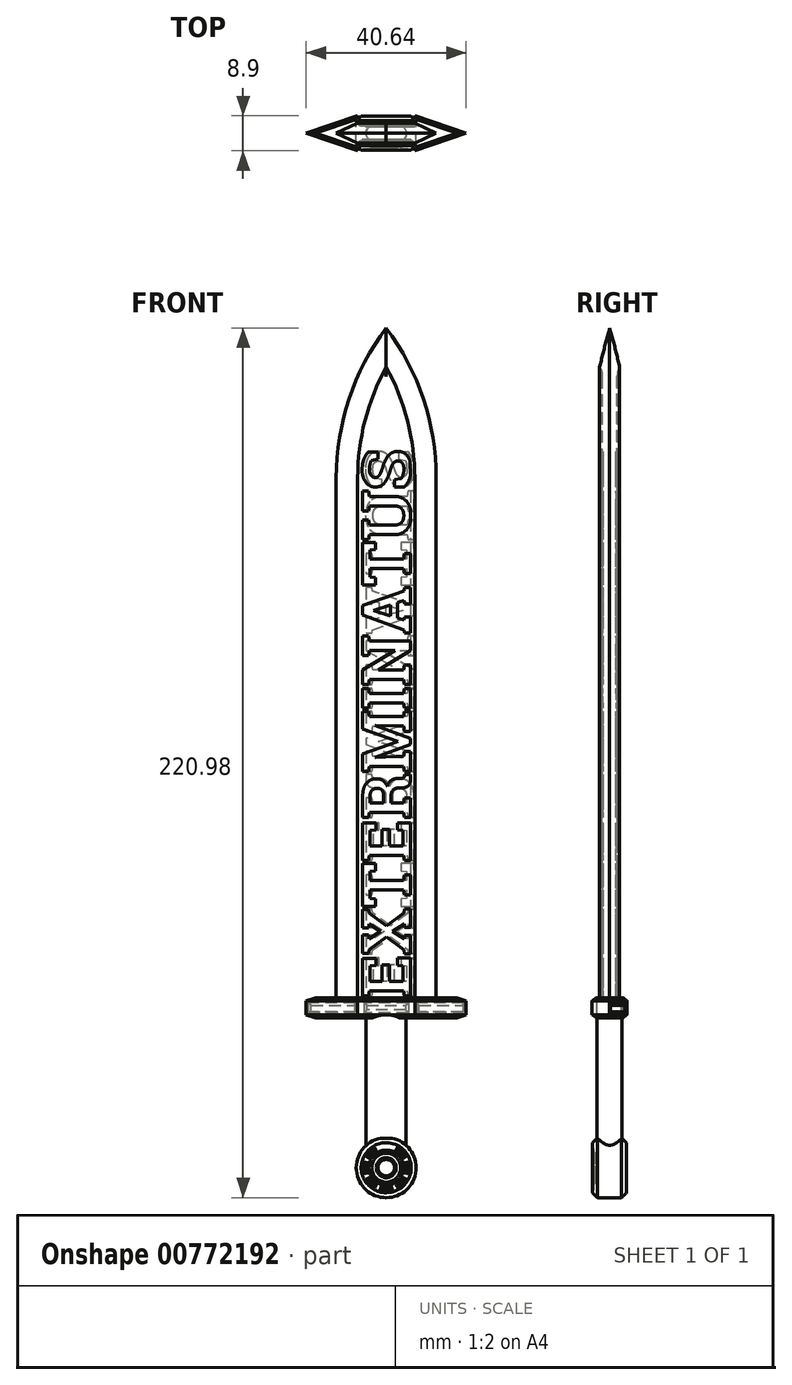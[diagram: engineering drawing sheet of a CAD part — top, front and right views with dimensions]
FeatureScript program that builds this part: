
annotation { "Feature Type Name" : "Feature", "Feature Type Description" : "" }
export const myFeature = defineFeature(function(context is Context, id is Id, definition is map)
    precondition{}
    {
        {
            var Q0;
            Q0=qCreatedBy(makeId("Front.planeOp"),FACE);
            var sketch = newSketch(context, id + "F0", { "sketchPlane" : qUnion([Q0])});
            skLineSegment(sketch, "E0.bottom", {"start": v(-51.68, 0) * mm, "end": v(-26.28, 0) * mm});
            skLineSegment(sketch, "E0.top", {"start": v(-51.68, 132.08) * mm, "end": v(-26.28, 132.08) * mm});
            skLineSegment(sketch, "E0.left", {"start": v(-51.68, 0) * mm, "end": v(-51.68, 132.08) * mm});
            skLineSegment(sketch, "E0.right", {"start": v(-26.28, 0) * mm, "end": v(-26.28, 132.08) * mm});
            skLineSegment(sketch, "E1", {"start": v(-38.98, 132.08) * mm, "end": v(-38.98, 170.18) * mm});
            skArc(sketch, "E2", {"start": v(-38.98, 170.18) * mm, "mid": v(-48.42, 152.16) * mm, "end": v(-51.68, 132.08) * mm});
            skArc(sketch, "E3", {"start": v(-26.28, 132.08) * mm, "mid": v(-29.54, 152.16) * mm, "end": v(-38.98, 170.18) * mm});
            skSolve(sketch);
        }
        {
            var Q0;
            Q0 = qSketchRegion(id + "F0", true);
            extrude(context, id + "F1", {"entities" : qUnion([Q0]), "endBound" : BoundingType.SYMMETRIC, "oppositeDirection" : true, "depth" : 5.08 * mm, "offsetDistance" : 25.4 * mm});
        }
        {
            var Q0;
            Q0=makeQuery(id+"F1.opExtrude","CAP_EDGE",EDGE,{"disambiguationData":[OSD([sQuery(id+"F0.wireOp",EDGE,"E3")])],"isStart":true});
            var Q1;
            Q1=makeQuery(id+"F1.opExtrude","CAP_EDGE",EDGE,{"disambiguationData":[OSD([sQuery(id+"F0.wireOp",EDGE,"E2")])],"isStart":true});
            chamfer(context, id + "F2", {"entities" : qUnion([Q0, Q1]), "chamferType" : ChamferType.OFFSET_ANGLE, "width" : 2.54 * mm, "oppositeDirection" : true, "angle" : 65 * degree, "tangentPropagation" : true});
        }
        {
            var Q0;
            Q0=makeQuery(id+"F1.opExtrude","CAP_EDGE",EDGE,{"disambiguationData":[OSD([sQuery(id+"F0.wireOp",EDGE,"E3")])],"isStart":false});
            var Q1;
            Q1=makeQuery(id+"F1.opExtrude","CAP_EDGE",EDGE,{"disambiguationData":[OSD([sQuery(id+"F0.wireOp",EDGE,"E2")])],"isStart":false});
            chamfer(context, id + "F3", {"entities" : qUnion([Q0, Q1]), "chamferType" : ChamferType.OFFSET_ANGLE, "width" : 2.54 * mm, "oppositeDirection" : false, "angle" : 65 * degree, "tangentPropagation" : true});
        }
        {
            var Q0;
            Q0=makeQuery(id+"F1.opExtrude","CAP_FACE",FACE,{"disambiguationData":[OSD([sQuery(id+"F0.wireOp",EDGE,"E0.bottom"),sQuery(id+"F0.wireOp",EDGE,"E0.left"),sQuery(id+"F0.wireOp",EDGE,"E0.right"),sQuery(id+"F0.wireOp",EDGE,"E2"),sQuery(id+"F0.wireOp",EDGE,"E3")])],"isStart":false});
            var sketch = newSketch(context, id + "F4", { "sketchPlane" : qUnion([Q0])});
            skLineSegment(sketch, "E4.0.0", {"start": v(31.72, 0) * mm, "end": v(46.23, 0) * mm});
            skLineSegment(sketch, "E4.0.1", {"start": v(46.23, 0) * mm, "end": v(46.23, 132.08) * mm});
            skArc(sketch, "E4.0.2", {"start": v(46.23, 132.08) * mm, "mid": v(44.39, 146.59) * mm, "end": v(38.98, 160.18) * mm});
            skArc(sketch, "E4.0.3", {"start": v(38.98, 160.18) * mm, "mid": v(33.57, 146.59) * mm, "end": v(31.72, 132.08) * mm});
            skLineSegment(sketch, "E4.0.4", {"start": v(31.72, 132.08) * mm, "end": v(31.72, 0) * mm});
            skSolve(sketch);
        }
        {
            var Q0;
            Q0 = qSketchRegion(id + "F4", true);
            extrude(context, id + "F5", {"entities" : qUnion([Q0]), "operationType" : NewBodyOperationType.REMOVE, "oppositeDirection" : true, "depth" : 0.64 * mm, "offsetDistance" : 25.4 * mm});
        }
        {
            var Q0;
            Q0=makeQuery(id+"F1.opExtrude","CAP_FACE",FACE,{"disambiguationData":[OSD([sQuery(id+"F0.wireOp",EDGE,"E0.bottom"),sQuery(id+"F0.wireOp",EDGE,"E0.left"),sQuery(id+"F0.wireOp",EDGE,"E0.right"),sQuery(id+"F0.wireOp",EDGE,"E2"),sQuery(id+"F0.wireOp",EDGE,"E3")])],"isStart":true});
            var sketch = newSketch(context, id + "F6", { "sketchPlane" : qUnion([Q0])});
            skArc(sketch, "E5.0.0", {"start": v(-38.98, 160.18) * mm, "mid": v(-44.39, 146.59) * mm, "end": v(-46.23, 132.08) * mm});
            skLineSegment(sketch, "E5.0.1", {"start": v(-46.23, 132.08) * mm, "end": v(-46.23, 0) * mm});
            skLineSegment(sketch, "E5.0.2", {"start": v(-46.23, 0) * mm, "end": v(-31.72, 0) * mm});
            skLineSegment(sketch, "E5.0.3", {"start": v(-31.72, 0) * mm, "end": v(-31.72, 132.08) * mm});
            skArc(sketch, "E5.0.4", {"start": v(-31.72, 132.08) * mm, "mid": v(-33.57, 146.59) * mm, "end": v(-38.98, 160.18) * mm});
            skSolve(sketch);
        }
        {
            var Q0;
            Q0 = qSketchRegion(id + "F6", true);
            extrude(context, id + "F7", {"entities" : qUnion([Q0]), "operationType" : NewBodyOperationType.REMOVE, "oppositeDirection" : true, "depth" : 0.64 * mm, "offsetDistance" : 25.4 * mm});
        }
        {
            var Q0;
            Q0=makeQuery(id+"F7.boolean.opBoolean","COPY",EDGE,{"derivedFrom":makeQuery(id+"F7.opExtrude","CAP_EDGE",EDGE,{"disambiguationData":[OSD([sQuery(id+"F6.wireOp",EDGE,"E5.0.3")])],"isStart":false})});
            var Q1;
            Q1=makeQuery(id+"F7.boolean.opBoolean","COPY",EDGE,{"derivedFrom":makeQuery(id+"F7.opExtrude","CAP_EDGE",EDGE,{"disambiguationData":[OSD([sQuery(id+"F6.wireOp",EDGE,"E5.0.1")])],"isStart":false})});
            fillet(context, id + "F8", {"entities" : qUnion([Q0, Q1]), "radius" : 1.27 * mm, "tangentPropagation" : true, "allowEdgeOverflow" : false});
        }
        {
            var Q0;
            Q0=makeQuery(id+"F5.boolean.opBoolean","COPY",EDGE,{"derivedFrom":makeQuery(id+"F5.opExtrude","CAP_EDGE",EDGE,{"disambiguationData":[OSD([sQuery(id+"F4.wireOp",EDGE,"E4.0.1")])],"isStart":false})});
            var Q1;
            Q1=makeQuery(id+"F5.boolean.opBoolean","COPY",EDGE,{"derivedFrom":makeQuery(id+"F5.opExtrude","CAP_EDGE",EDGE,{"disambiguationData":[OSD([sQuery(id+"F4.wireOp",EDGE,"E4.0.4")])],"isStart":false})});
            fillet(context, id + "F9", {"entities" : qUnion([Q0, Q1]), "radius" : 1.27 * mm, "tangentPropagation" : true, "allowEdgeOverflow" : false});
        }
        {
            var Q0;
            Q0=makeQuery(id+"F7.boolean.opBoolean","COPY",FACE,{"derivedFrom":makeQuery(id+"F7.opExtrude","CAP_FACE",FACE,{"disambiguationData":[OSD([sQuery(id+"F6.wireOp",EDGE,"E5.0.0"),sQuery(id+"F6.wireOp",EDGE,"E5.0.1"),sQuery(id+"F6.wireOp",EDGE,"E5.0.2"),sQuery(id+"F6.wireOp",EDGE,"E5.0.3"),sQuery(id+"F6.wireOp",EDGE,"E5.0.4")])],"isStart":false})});
            var sketch = newSketch(context, id + "F10", { "sketchPlane" : qUnion([Q0])});
            skText(sketch, "E6", { "text": "EXTERMINATUS\n", "fontName": "RobotoSlab-Bold.ttf"});
            const initialGuessF10  = {"E6": [-0.03282, 0, 0, 1, 0.0123]};
            skSetInitialGuess(sketch, initialGuessF10);
            skSolve(sketch);
        }
        {
            var Q0;
            Q0 = qSketchRegion(id + "F10", true);
            extrude(context, id + "F11", {"entities" : qUnion([Q0]), "operationType" : NewBodyOperationType.REMOVE, "oppositeDirection" : true, "depth" : 0.25 * mm, "offsetDistance" : 25.4 * mm});
        }
        {
            var Q0;
            Q0=makeQuery(id+"F5.boolean.opBoolean","COPY",FACE,{"derivedFrom":makeQuery(id+"F5.opExtrude","CAP_FACE",FACE,{"disambiguationData":[OSD([sQuery(id+"F4.wireOp",EDGE,"E4.0.0"),sQuery(id+"F4.wireOp",EDGE,"E4.0.1"),sQuery(id+"F4.wireOp",EDGE,"E4.0.2"),sQuery(id+"F4.wireOp",EDGE,"E4.0.3"),sQuery(id+"F4.wireOp",EDGE,"E4.0.4")])],"isStart":false})});
            var sketch = newSketch(context, id + "F12", { "sketchPlane" : qUnion([Q0])});
            skText(sketch, "E7", { "text": "EXTERMINATUS", "fontName": "RobotoSlab-Bold.ttf"});
            const initialGuessF12  = {"E7": [0.04408, 0, 0, 1, 0.0123]};
            skSetInitialGuess(sketch, initialGuessF12);
            skSolve(sketch);
        }
        {
            var Q0;
            Q0 = qSketchRegion(id + "F12", true);
            extrude(context, id + "F13", {"entities" : qUnion([Q0]), "operationType" : NewBodyOperationType.REMOVE, "oppositeDirection" : true, "depth" : 0.25 * mm, "offsetDistance" : 25.4 * mm});
        }
        {
            var Q0;
            Q0=makeQuery(id+"F1.opExtrude","SWEPT_FACE",FACE,{"disambiguationData":[OSD([sQuery(id+"F0.wireOp",EDGE,"E0.bottom")])]});
            var sketch = newSketch(context, id + "F14", { "sketchPlane" : qUnion([Q0])});
            skLineSegment(sketch, "E8.0.0", {"start": v(-32.82, 1.9) * mm, "end": v(-45.13, 1.9) * mm});
            skArc(sketch, "E8.0.1", {"start": v(-45.13, 1.9) * mm, "mid": v(-45.77, 2.08) * mm, "end": v(-46.23, 2.54) * mm});
            skLineSegment(sketch, "E8.0.2", {"start": v(-46.23, 2.54) * mm, "end": v(-51.68, 0) * mm});
            skLineSegment(sketch, "E8.0.3", {"start": v(-51.68, 0) * mm, "end": v(-46.23, -2.54) * mm});
            skArc(sketch, "E8.0.4", {"start": v(-46.23, -2.54) * mm, "mid": v(-45.77, -2.08) * mm, "end": v(-45.13, -1.9) * mm});
            skLineSegment(sketch, "E8.0.5", {"start": v(-45.13, -1.9) * mm, "end": v(-32.82, -1.9) * mm});
            skArc(sketch, "E8.0.6", {"start": v(-32.82, -1.9) * mm, "mid": v(-32.19, -2.08) * mm, "end": v(-31.72, -2.54) * mm});
            skLineSegment(sketch, "E8.0.7", {"start": v(-31.72, -2.54) * mm, "end": v(-26.28, 0) * mm});
            skLineSegment(sketch, "E8.0.8", {"start": v(-26.28, 0) * mm, "end": v(-31.72, 2.54) * mm});
            skArc(sketch, "E8.0.9", {"start": v(-31.72, 2.54) * mm, "mid": v(-32.19, 2.08) * mm, "end": v(-32.82, 1.9) * mm});
            skLineSegment(sketch, "E9.bottom", {"start": v(-59.3, -4.45) * mm, "end": v(-18.66, -4.44) * mm});
            skLineSegment(sketch, "E9.top", {"start": v(-59.3, 4.45) * mm, "end": v(-18.66, 4.45) * mm});
            skLineSegment(sketch, "E9.left", {"start": v(-59.3, -4.45) * mm, "end": v(-59.3, 4.45) * mm});
            skLineSegment(sketch, "E9.right", {"start": v(-18.66, -4.44) * mm, "end": v(-18.66, 4.45) * mm});
            skPoint(sketch, "E10.start.orphan", {"position": v(-59.3, 0) * mm});
            skLineSegment(sketch, "E11", {"start": v(-59.3, 0) * mm, "end": v(-46.23, 4.45) * mm});
            skLineSegment(sketch, "E12", {"start": v(-38.98, 1.9) * mm, "end": v(-38.98, 0.5) * mm});
            skLineSegment(sketch, "E13", {"start": v(-43.87, 0) * mm, "end": v(-41.2, 0) * mm});
            skLineSegment(sketch, "E14", {"start": v(-45.13, 3.18) * mm, "end": v(-32.82, 3.18) * mm});
            skLineSegment(sketch, "E15", {"start": v(-32.82, -3.18) * mm, "end": v(-45.13, -3.18) * mm});
            skLineSegment(sketch, "E16.MirrorCS", {"start": v(-18.66, 0) * mm, "end": v(-31.72, 4.45) * mm});
            skArc(sketch, "E17", {"start": v(-46.23, 4.45) * mm, "mid": v(-45.97, 3.56) * mm, "end": v(-45.13, 3.18) * mm});
            skArc(sketch, "E18.MirrorCS", {"start": v(-31.72, 4.45) * mm, "mid": v(-31.98, 3.56) * mm, "end": v(-32.82, 3.18) * mm});
            skArc(sketch, "E19.MirrorCS", {"start": v(-46.23, -4.45) * mm, "mid": v(-45.97, -3.56) * mm, "end": v(-45.13, -3.18) * mm});
            skArc(sketch, "E20.MirrorCS", {"start": v(-31.72, -4.45) * mm, "mid": v(-31.98, -3.56) * mm, "end": v(-32.82, -3.18) * mm});
            skLineSegment(sketch, "E21.MirrorCS", {"start": v(-59.3, 0) * mm, "end": v(-46.23, -4.45) * mm});
            skLineSegment(sketch, "E22.MirrorCS", {"start": v(-18.66, 0) * mm, "end": v(-31.72, -4.45) * mm});
            skSolve(sketch);
        }
        {
            var Q0;
            {var subQ0=sQuery(id+"F14.wireOp",EDGE,"E8.0.1");Q0=makeQuery(id+"F14.imprint","IMPRINT",FACE,{"disambiguationData":[TD([[makeQuery(id+"F14.imprint","IMPRINT",EDGE,{"derivedFrom":subQ0}),-1.0]])]});}
            var Q1;
            {var subQ0=sQuery(id+"F14.wireOp",EDGE,"E8.0.1");Q1=makeQuery(id+"F14.imprint","IMPRINT",FACE,{"disambiguationData":[TD([[makeQuery(id+"F14.imprint","IMPRINT",EDGE,{"derivedFrom":subQ0}),1.0]])]});}
            extrude(context, id + "F15", {"entities" : qUnion([Q0, Q1]), "operationType" : NewBodyOperationType.ADD, "depth" : 5.08 * mm, "offsetDistance" : 25.4 * mm});
        }
        {
            var Q0;
            Q0=makeQuery(id+"F15.opExtrude","CAP_EDGE",EDGE,{"disambiguationData":[OSD([sQuery(id+"F14.wireOp",EDGE,"E22.MirrorCS")])],"isStart":true});
            var Q1;
            Q1=makeQuery(id+"F15.opExtrude","CAP_EDGE",EDGE,{"disambiguationData":[OSD([sQuery(id+"F14.wireOp",EDGE,"E15")])],"isStart":true});
            var Q2;
            Q2=makeQuery(id+"F15.opExtrude","CAP_EDGE",EDGE,{"disambiguationData":[OSD([sQuery(id+"F14.wireOp",EDGE,"E21.MirrorCS")])],"isStart":true});
            var Q3;
            Q3=makeQuery(id+"F15.opExtrude","CAP_EDGE",EDGE,{"disambiguationData":[OSD([sQuery(id+"F14.wireOp",EDGE,"E11")])],"isStart":true});
            var Q4;
            Q4=makeQuery(id+"F15.opExtrude","CAP_EDGE",EDGE,{"disambiguationData":[OSD([sQuery(id+"F14.wireOp",EDGE,"E14")])],"isStart":true});
            var Q5;
            Q5=makeQuery(id+"F15.opExtrude","CAP_EDGE",EDGE,{"disambiguationData":[OSD([sQuery(id+"F14.wireOp",EDGE,"E16.MirrorCS")])],"isStart":true});
            var Q6;
            Q6=makeQuery(id+"F15.opExtrude","CAP_FACE",FACE,{"disambiguationData":[OSD([sQuery(id+"F14.wireOp",EDGE,"E11"),sQuery(id+"F14.wireOp",EDGE,"E14"),sQuery(id+"F14.wireOp",EDGE,"E15"),sQuery(id+"F14.wireOp",EDGE,"E16.MirrorCS"),sQuery(id+"F14.wireOp",EDGE,"E17"),sQuery(id+"F14.wireOp",EDGE,"E18.MirrorCS"),sQuery(id+"F14.wireOp",EDGE,"E19.MirrorCS"),sQuery(id+"F14.wireOp",EDGE,"E20.MirrorCS"),sQuery(id+"F14.wireOp",EDGE,"E21.MirrorCS"),sQuery(id+"F14.wireOp",EDGE,"E22.MirrorCS")])],"isStart":false});
            chamfer(context, id + "F16", {"entities" : qUnion([Q0, Q1, Q2, Q3, Q4, Q5, Q6]), "width" : 0.76 * mm, "tangentPropagation" : true});
        }
        {
            var Q0;
            Q0=makeQuery(id+"F15.opExtrude","CAP_FACE",FACE,{"disambiguationData":[OSD([sQuery(id+"F14.wireOp",EDGE,"E11"),sQuery(id+"F14.wireOp",EDGE,"E14"),sQuery(id+"F14.wireOp",EDGE,"E15"),sQuery(id+"F14.wireOp",EDGE,"E16.MirrorCS"),sQuery(id+"F14.wireOp",EDGE,"E17"),sQuery(id+"F14.wireOp",EDGE,"E18.MirrorCS"),sQuery(id+"F14.wireOp",EDGE,"E19.MirrorCS"),sQuery(id+"F14.wireOp",EDGE,"E20.MirrorCS"),sQuery(id+"F14.wireOp",EDGE,"E21.MirrorCS"),sQuery(id+"F14.wireOp",EDGE,"E22.MirrorCS")])],"isStart":false});
            var sketch = newSketch(context, id + "F17", { "sketchPlane" : qUnion([Q0])});
            skArc(sketch, "E23.0.0", {"start": v(-32.82, -2.41) * mm, "mid": v(-31.84, -2.7) * mm, "end": v(-31.15, -3.44) * mm});
            skLineSegment(sketch, "E23.0.1", {"start": v(-31.15, -3.44) * mm, "end": v(-21.02, 0) * mm});
            skLineSegment(sketch, "E23.0.2", {"start": v(-21.02, 0) * mm, "end": v(-31.15, 3.44) * mm});
            skArc(sketch, "E23.0.3", {"start": v(-31.15, 3.44) * mm, "mid": v(-31.84, 2.7) * mm, "end": v(-32.82, 2.41) * mm});
            skLineSegment(sketch, "E23.0.4", {"start": v(-32.82, 2.41) * mm, "end": v(-45.13, 2.41) * mm});
            skArc(sketch, "E23.0.5", {"start": v(-45.13, 2.41) * mm, "mid": v(-46.11, 2.7) * mm, "end": v(-46.8, 3.44) * mm});
            skLineSegment(sketch, "E23.0.6", {"start": v(-46.8, 3.44) * mm, "end": v(-56.93, 0) * mm});
            skLineSegment(sketch, "E23.0.7", {"start": v(-56.93, 0) * mm, "end": v(-46.8, -3.44) * mm});
            skArc(sketch, "E23.0.8", {"start": v(-46.8, -3.44) * mm, "mid": v(-46.11, -2.7) * mm, "end": v(-45.13, -2.41) * mm});
            skLineSegment(sketch, "E23.0.9", {"start": v(-45.13, -2.41) * mm, "end": v(-32.82, -2.41) * mm});
            skPoint(sketch, "E24.centerSnap0", {"position": v(-38.98, -2.41) * mm});
            skPoint(sketch, "E24.center.orphan", {"position": v(-38.98, 0) * mm});
            skEllipse(sketch, "E25", {"center": v(-38.98, 0) * mm, "majorRadius": 5.08 * mm, "minorRadius": 3.18 * mm, "majorAxis": v(-1, 0)});
            skSolve(sketch);
        }
        {
            var Q0;
            {var subQ0=sQuery(id+"F17.wireOp",EDGE,"E25");var subQ1=sQuery(id+"F17.wireOp",EDGE,"E23.0.4");var subQ2=makeQuery(id+"F17.imprint","INTERSECT",VERTEX,{"disambiguationData":[OD(0.0)],"derivedFrom":[subQ1,subQ0]});Q0=makeQuery(id+"F17.imprint","IMPRINT",FACE,{"disambiguationData":[TD([[makeQuery(id+"F17.imprint","IMPRINT",EDGE,{"disambiguationData":[TD([[subQ2,-1.0]])],"derivedFrom":subQ1}),1.0]])]});}
            var Q1;
            {var subQ0=sQuery(id+"F17.wireOp",EDGE,"E25");var subQ1=sQuery(id+"F17.wireOp",EDGE,"E23.0.4");var subQ2=makeQuery(id+"F17.imprint","INTERSECT",VERTEX,{"disambiguationData":[OD(0.0)],"derivedFrom":[subQ1,subQ0]});Q1=makeQuery(id+"F17.imprint","IMPRINT",FACE,{"disambiguationData":[TD([[makeQuery(id+"F17.imprint","IMPRINT",EDGE,{"disambiguationData":[TD([[subQ2,-1.0]])],"derivedFrom":subQ1}),-1.0]])]});}
            var Q2;
            {var subQ0=sQuery(id+"F17.wireOp",EDGE,"E25");var subQ1=sQuery(id+"F17.wireOp",EDGE,"E23.0.9");var subQ2=makeQuery(id+"F17.imprint","INTERSECT",VERTEX,{"disambiguationData":[OD(0.0)],"derivedFrom":[subQ1,subQ0]});Q2=makeQuery(id+"F17.imprint","IMPRINT",FACE,{"disambiguationData":[TD([[makeQuery(id+"F17.imprint","IMPRINT",EDGE,{"disambiguationData":[TD([[subQ2,-1.0]])],"derivedFrom":subQ1}),-1.0]])]});}
            extrude(context, id + "F18", {"entities" : qUnion([Q0, Q1, Q2]), "operationType" : NewBodyOperationType.ADD, "depth" : 38.1 * mm, "offsetDistance" : 25.4 * mm});
        }
        {
            var Q0;
            {var subQ0=sQuery(id+"F14.wireOp",EDGE,"E14");var subQ1=sQuery(id+"F17.wireOp",EDGE,"E25");Q0=makeQuery(id+"F18.boolean.opBoolean","SPLIT",FACE,{"disambiguationData":[TD([makeQuery(id+"F16.opChamfer","BLEND_FACE",FACE,{"disambiguationData":[OSD([subQ0]),TDD([makeQuery(id+"F15.opExtrude","CAP_EDGE",EDGE,{"disambiguationData":[OSD([subQ0])],"isStart":false})])]})])],"derivedFrom":makeQuery(id+"F18.opExtrude","CAP_FACE",FACE,{"disambiguationData":[OSD([subQ1])],"isStart":true})});}
            var sketch = newSketch(context, id + "F19", { "sketchPlane" : qUnion([Q0])});
            skEllipticalArc(sketch, "E26.0", {});
            skLineSegment(sketch, "E27.0.1", {"start": v(-35.68, -2.41) * mm, "end": v(-42.28, -2.41) * mm});
            skEllipticalArc(sketch, "E28.0.0", {});
            skLineSegment(sketch, "E28.0.1", {"start": v(-42.28, 2.41) * mm, "end": v(-35.68, 2.41) * mm});
            const initialGuessF19  = {"E26.0": [-0.03897777617146298, 0, -1, 0, 0.00508, 0.003175, 0.8633131150155545, 2.278279538574239], "E26.0": [-0.03897777617146298, 0, -1, 0, 0.00508, 0.003175, 0.8633131150155545, 2.278279538574239], "E28.0.0": [-0.03897777617146298, 0, -1, 0, 0.00508, 0.003175, 4.004905768605347, 5.419872192164032]};
            skSetInitialGuess(sketch, initialGuessF19);
            skSolve(sketch);
        }
        {
            var Q0;
            Q0 = qSketchRegion(id + "F19", true);
            extrude(context, id + "F20", {"entities" : qUnion([Q0]), "operationType" : NewBodyOperationType.ADD, "depth" : 0.76 * mm, "offsetDistance" : 25.4 * mm});
        }
        {
            var Q0;
            Q0=makeQuery(id+"F15.opExtrude","SWEPT_FACE",FACE,{"disambiguationData":[OSD([sQuery(id+"F14.wireOp",EDGE,"E15")])]});
            var sketch = newSketch(context, id + "F21", { "sketchPlane" : qUnion([Q0])});
            skLineSegment(sketch, "E29.0.0", {"start": v(32.82, -0.76) * mm, "end": v(32.82, -4.32) * mm});
            skLineSegment(sketch, "E29.0.1", {"start": v(32.82, -4.32) * mm, "end": v(38.98, -4.32) * mm});
            skLineSegment(sketch, "E29.0.2", {"start": v(38.98, -4.32) * mm, "end": v(45.13, -4.32) * mm});
            skLineSegment(sketch, "E29.0.3", {"start": v(45.13, -4.32) * mm, "end": v(45.13, -0.76) * mm});
            skLineSegment(sketch, "E29.0.4", {"start": v(45.13, -0.76) * mm, "end": v(32.82, -0.76) * mm});
            skLineSegment(sketch, "E30.bottom", {"start": v(33.33, -1.27) * mm, "end": v(44.62, -1.27) * mm});
            skLineSegment(sketch, "E30.top", {"start": v(33.33, -3.81) * mm, "end": v(44.62, -3.8) * mm});
            skLineSegment(sketch, "E30.left", {"start": v(33.33, -1.27) * mm, "end": v(33.33, -3.81) * mm});
            skLineSegment(sketch, "E30.right", {"start": v(44.62, -1.27) * mm, "end": v(44.62, -3.8) * mm});
            skSolve(sketch);
        }
        {
            var Q0;
            Q0=makeQuery(id+"F21.imprint","IMPRINT",FACE,{"disambiguationData":[TD([[makeQuery(id+"F21.imprint","IMPRINT",EDGE,{"derivedFrom":sQuery(id+"F21.wireOp",EDGE,"E30.bottom")}),-1.0]])]});
            extrude(context, id + "F22", {"entities" : qUnion([Q0]), "operationType" : NewBodyOperationType.REMOVE, "oppositeDirection" : true, "depth" : 0.25 * mm, "offsetDistance" : 25.4 * mm});
        }
        {
            var Q0;
            Q0=makeQuery(id+"F15.opExtrude","SWEPT_FACE",FACE,{"disambiguationData":[OSD([sQuery(id+"F14.wireOp",EDGE,"E22.MirrorCS")])]});
            var sketch = newSketch(context, id + "F23", { "sketchPlane" : qUnion([Q0])});
            skLineSegment(sketch, "E31.bottom", {"start": v(18.17, -1.27) * mm, "end": v(30.96, -1.27) * mm});
            skLineSegment(sketch, "E31.top", {"start": v(18.17, -3.81) * mm, "end": v(30.96, -3.81) * mm});
            skLineSegment(sketch, "E31.left", {"start": v(18.17, -1.27) * mm, "end": v(18.17, -3.81) * mm});
            skLineSegment(sketch, "E31.right", {"start": v(30.96, -1.27) * mm, "end": v(30.96, -3.81) * mm});
            skSolve(sketch);
        }
        {
            var Q0;
            Q0 = qSketchRegion(id + "F23", true);
            extrude(context, id + "F24", {"entities" : qUnion([Q0]), "operationType" : NewBodyOperationType.REMOVE, "oppositeDirection" : true, "depth" : 0.25 * mm, "offsetDistance" : 25.4 * mm});
        }
        {
            var Q0;
            Q0=makeQuery(id+"F15.opExtrude","SWEPT_FACE",FACE,{"disambiguationData":[OSD([sQuery(id+"F14.wireOp",EDGE,"E21.MirrorCS")])]});
            var sketch = newSketch(context, id + "F25", { "sketchPlane" : qUnion([Q0])});
            skLineSegment(sketch, "E32.bottom", {"start": v(42.84, -1.27) * mm, "end": v(55.63, -1.27) * mm});
            skLineSegment(sketch, "E32.top", {"start": v(42.84, -3.81) * mm, "end": v(55.63, -3.8) * mm});
            skLineSegment(sketch, "E32.left", {"start": v(42.84, -1.27) * mm, "end": v(42.84, -3.81) * mm});
            skLineSegment(sketch, "E32.right", {"start": v(55.63, -1.27) * mm, "end": v(55.63, -3.8) * mm});
            skSolve(sketch);
        }
        {
            var Q0;
            Q0 = qSketchRegion(id + "F25", true);
            extrude(context, id + "F26", {"entities" : qUnion([Q0]), "operationType" : NewBodyOperationType.REMOVE, "oppositeDirection" : true, "depth" : 0.25 * mm, "offsetDistance" : 25.4 * mm});
        }
        {
            var Q0;
            Q0=makeQuery(id+"F22.boolean.opBoolean","COPY",FACE,{"derivedFrom":makeQuery(id+"F22.opExtrude","CAP_FACE",FACE,{"disambiguationData":[OSD([sQuery(id+"F21.wireOp",EDGE,"E30.bottom"),sQuery(id+"F21.wireOp",EDGE,"E30.top"),sQuery(id+"F21.wireOp",EDGE,"E30.left"),sQuery(id+"F21.wireOp",EDGE,"E30.right")])],"isStart":false})});
            var Q1;
            Q1=makeQuery(id+"F26.boolean.opBoolean","COPY",FACE,{"derivedFrom":makeQuery(id+"F26.opExtrude","CAP_FACE",FACE,{"disambiguationData":[OSD([sQuery(id+"F25.wireOp",EDGE,"E32.bottom"),sQuery(id+"F25.wireOp",EDGE,"E32.top"),sQuery(id+"F25.wireOp",EDGE,"E32.left"),sQuery(id+"F25.wireOp",EDGE,"E32.right")])],"isStart":false})});
            var Q2;
            Q2=makeQuery(id+"F24.boolean.opBoolean","COPY",FACE,{"derivedFrom":makeQuery(id+"F24.opExtrude","CAP_FACE",FACE,{"disambiguationData":[OSD([sQuery(id+"F23.wireOp",EDGE,"E31.bottom"),sQuery(id+"F23.wireOp",EDGE,"E31.top"),sQuery(id+"F23.wireOp",EDGE,"E31.left"),sQuery(id+"F23.wireOp",EDGE,"E31.right")])],"isStart":false})});
            chamfer(context, id + "F27", {"entities" : qUnion([Q0, Q1, Q2]), "chamferType" : ChamferType.OFFSET_ANGLE, "width" : 0.25 * mm, "oppositeDirection" : false, "angle" : 70 * degree, "tangentPropagation" : true});
        }
        {
            var Q0;
            Q0=qCreatedBy(makeId("Front.planeOp"),FACE);
            var sketch = newSketch(context, id + "F28", { "sketchPlane" : qUnion([Q0])});
            skLineSegment(sketch, "E33.0", {"start": v(-33.9, -43.18) * mm, "end": v(-44.06, -43.18) * mm});
            skCircle(sketch, "E34", {"center": v(-38.98, -43.18) * mm, "radius": 7.62 * mm});
            skSolve(sketch);
        }
        {
            var Q0;
            Q0 = qSketchRegion(id + "F28", true);
            extrude(context, id + "F29", {"entities" : qUnion([Q0]), "operationType" : NewBodyOperationType.ADD, "endBound" : BoundingType.SYMMETRIC, "depth" : 8.64 * mm, "offsetDistance" : 25.4 * mm});
        }
        {
            var Q0;
            Q0=makeQuery(id+"F29.opExtrude","CAP_EDGE",EDGE,{"disambiguationData":[OSD([sQuery(id+"F28.wireOp",EDGE,"E34")])],"isStart":true});
            var Q1;
            Q1=makeQuery(id+"F29.opExtrude","CAP_EDGE",EDGE,{"disambiguationData":[OSD([sQuery(id+"F28.wireOp",EDGE,"E34")])],"isStart":false});
            chamfer(context, id + "F30", {"entities" : qUnion([Q0, Q1]), "width" : 1.27 * mm, "tangentPropagation" : true});
        }
        {
            var Q0;
            Q0=makeQuery(id+"F29.opExtrude","CAP_FACE",FACE,{"disambiguationData":[OSD([sQuery(id+"F28.wireOp",EDGE,"E34")])],"isStart":false});
            var sketch = newSketch(context, id + "F31", { "sketchPlane" : qUnion([Q0])});
            skCircle(sketch, "E35.0.0", {"center": v(-38.98, -43.18) * mm, "radius": 6.35 * mm});
            skCircle(sketch, "E36", {"center": v(-38.98, -43.18) * mm, "radius": 4.45 * mm});
            skSolve(sketch);
        }
        {
            var Q0;
            Q0=makeQuery(id+"F31.imprint","IMPRINT",FACE,{"disambiguationData":[TD([[makeQuery(id+"F31.imprint","IMPRINT",EDGE,{"derivedFrom":sQuery(id+"F31.wireOp",EDGE,"E36")}),1.0]])]});
            extrude(context, id + "F32", {"entities" : qUnion([Q0]), "operationType" : NewBodyOperationType.REMOVE, "oppositeDirection" : true, "depth" : 0.76 * mm, "offsetDistance" : 25.4 * mm});
        }
        {
            var Q0;
            Q0=makeQuery(id+"F32.boolean.opBoolean","COPY",EDGE,{"derivedFrom":makeQuery(id+"F32.opExtrude","CAP_EDGE",EDGE,{"disambiguationData":[OSD([sQuery(id+"F31.wireOp",EDGE,"E36")])],"isStart":false})});
            chamfer(context, id + "F33", {"entities" : qUnion([Q0]), "width" : 0.76 * mm, "tangentPropagation" : true});
        }
        {
            var Q0;
            Q0=makeQuery(id+"F32.boolean.opBoolean","COPY",FACE,{"derivedFrom":makeQuery(id+"F32.opExtrude","CAP_FACE",FACE,{"disambiguationData":[OSD([sQuery(id+"F31.wireOp",EDGE,"E36")])],"isStart":false})});
            var sketch = newSketch(context, id + "F34", { "sketchPlane" : qUnion([Q0])});
            skCircle(sketch, "E37.0.0", {"center": v(-38.98, -43.18) * mm, "radius": 3.68 * mm});
            skCircle(sketch, "E38", {"center": v(-38.98, -43.18) * mm, "radius": 2.54 * mm});
            skSolve(sketch);
        }
        {
            var Q0;
            Q0=makeQuery(id+"F34.imprint","IMPRINT",FACE,{"disambiguationData":[TD([[makeQuery(id+"F34.imprint","IMPRINT",EDGE,{"derivedFrom":sQuery(id+"F34.wireOp",EDGE,"E38")}),1.0]])]});
            extrude(context, id + "F35", {"entities" : qUnion([Q0]), "operationType" : NewBodyOperationType.ADD, "depth" : 0.76 * mm, "offsetDistance" : 25.4 * mm, "hasDraft" : true, "draftAngle" : 30 * degree, "draftPullDirection" : true});
        }
        {
            var Q0;
            Q0=makeQuery(id+"F29.opExtrude","CAP_FACE",FACE,{"disambiguationData":[OSD([sQuery(id+"F28.wireOp",EDGE,"E34")])],"isStart":false});
            var sketch = newSketch(context, id + "F36", { "sketchPlane" : qUnion([Q0])});
            skCircle(sketch, "E39.0.0", {"center": v(-38.98, -43.18) * mm, "radius": 2.1 * mm});
            skCircle(sketch, "E40", {"center": v(-38.98, -43.18) * mm, "radius": 5.97 * mm});
            skCircle(sketch, "E41", {"center": v(-38.98, -43.18) * mm, "radius": 4.83 * mm});
            skCircle(sketch, "E42.0", {"center": v(-38.98, -43.18) * mm, "radius": 6.35 * mm});
            skCircle(sketch, "E43.0", {"center": v(-38.98, -43.18) * mm, "radius": 4.44 * mm});
            skLineSegment(sketch, "E44", {"start": v(-40.52, -37.41) * mm, "end": v(-40.23, -38.52) * mm});
            skLineSegment(sketch, "E45.trimOffspring", {"start": v(-40.23, -38.52) * mm, "end": v(-40.52, -37.41) * mm});
            skLineSegment(sketch, "E46.trimOffspring", {"start": v(-37.73, -38.52) * mm, "end": v(-37.43, -37.41) * mm});
            skLineSegment(sketch, "E47.trimOffspring", {"start": v(-38.98, -36.83) * mm, "end": v(-38.98, -36.6) * mm});
            skLineSegment(sketch, "E48.1.0", {"start": v(-41.4, -39) * mm, "end": v(-41.96, -38.01) * mm});
            skLineSegment(sketch, "E48.1.1", {"start": v(-44.15, -40.2) * mm, "end": v(-43.16, -40.77) * mm});
            skLineSegment(sketch, "E48.2.0", {"start": v(-43.64, -41.93) * mm, "end": v(-44.74, -41.64) * mm});
            skLineSegment(sketch, "E48.2.1", {"start": v(-44.74, -44.72) * mm, "end": v(-43.64, -44.43) * mm});
            skLineSegment(sketch, "E48.3.0", {"start": v(-43.16, -45.6) * mm, "end": v(-44.15, -46.16) * mm});
            skLineSegment(sketch, "E48.3.1", {"start": v(-41.96, -48.35) * mm, "end": v(-41.4, -47.36) * mm});
            skLineSegment(sketch, "E48.4.0", {"start": v(-40.23, -47.84) * mm, "end": v(-40.52, -48.95) * mm});
            skLineSegment(sketch, "E48.4.1", {"start": v(-37.43, -48.95) * mm, "end": v(-37.73, -47.84) * mm});
            skLineSegment(sketch, "E48.5.0", {"start": v(-36.56, -47.36) * mm, "end": v(-36, -48.35) * mm});
            skLineSegment(sketch, "E48.5.1", {"start": v(-33.8, -46.16) * mm, "end": v(-34.8, -45.6) * mm});
            skLineSegment(sketch, "E48.6.0", {"start": v(-34.32, -44.43) * mm, "end": v(-33.21, -44.72) * mm});
            skLineSegment(sketch, "E48.6.1", {"start": v(-33.21, -41.64) * mm, "end": v(-34.32, -41.93) * mm});
            skLineSegment(sketch, "E48.7.0", {"start": v(-34.8, -40.77) * mm, "end": v(-33.8, -40.2) * mm});
            skLineSegment(sketch, "E48.7.1", {"start": v(-36, -38.01) * mm, "end": v(-36.56, -39) * mm});
            skSolve(sketch);
        }
        {
            var Q0;
            {var subQ0=sQuery(id+"F36.wireOp",EDGE,"E48.2.0");Q0=makeQuery(id+"F36.imprint","IMPRINT",FACE,{"disambiguationData":[TD([[makeQuery(id+"F36.imprint","IMPRINT",EDGE,{"derivedFrom":subQ0}),1.0]])]});}
            var Q1;
            {var subQ0=sQuery(id+"F36.wireOp",EDGE,"E48.1.0");Q1=makeQuery(id+"F36.imprint","IMPRINT",FACE,{"disambiguationData":[TD([[makeQuery(id+"F36.imprint","IMPRINT",EDGE,{"derivedFrom":subQ0}),1.0]])]});}
            var Q2;
            {var subQ0=sQuery(id+"F36.wireOp",EDGE,"E45.trimOffspring");Q2=makeQuery(id+"F36.imprint","IMPRINT",FACE,{"disambiguationData":[TD([[makeQuery(id+"F36.imprint","IMPRINT",EDGE,{"derivedFrom":subQ0}),-1.0]])]});}
            var Q3;
            {var subQ0=sQuery(id+"F36.wireOp",EDGE,"E48.7.0");Q3=makeQuery(id+"F36.imprint","IMPRINT",FACE,{"disambiguationData":[TD([[makeQuery(id+"F36.imprint","IMPRINT",EDGE,{"derivedFrom":subQ0}),1.0]])]});}
            var Q4;
            {var subQ0=sQuery(id+"F36.wireOp",EDGE,"E48.6.0");Q4=makeQuery(id+"F36.imprint","IMPRINT",FACE,{"disambiguationData":[TD([[makeQuery(id+"F36.imprint","IMPRINT",EDGE,{"derivedFrom":subQ0}),1.0]])]});}
            var Q5;
            {var subQ0=sQuery(id+"F36.wireOp",EDGE,"E48.5.0");Q5=makeQuery(id+"F36.imprint","IMPRINT",FACE,{"disambiguationData":[TD([[makeQuery(id+"F36.imprint","IMPRINT",EDGE,{"derivedFrom":subQ0}),1.0]])]});}
            var Q6;
            {var subQ0=sQuery(id+"F36.wireOp",EDGE,"E48.4.0");Q6=makeQuery(id+"F36.imprint","IMPRINT",FACE,{"disambiguationData":[TD([[makeQuery(id+"F36.imprint","IMPRINT",EDGE,{"derivedFrom":subQ0}),1.0]])]});}
            var Q7;
            {var subQ0=sQuery(id+"F36.wireOp",EDGE,"E48.3.0");Q7=makeQuery(id+"F36.imprint","IMPRINT",FACE,{"disambiguationData":[TD([[makeQuery(id+"F36.imprint","IMPRINT",EDGE,{"derivedFrom":subQ0}),1.0]])]});}
            extrude(context, id + "F37", {"entities" : qUnion([Q0, Q1, Q2, Q3, Q4, Q5, Q6, Q7]), "operationType" : NewBodyOperationType.REMOVE, "oppositeDirection" : true, "depth" : 0.25 * mm, "offsetDistance" : 25.4 * mm});
        }
        {
            var Q0;
            Q0=makeQuery(id+"F37.boolean.opBoolean","COPY",FACE,{"derivedFrom":makeQuery(id+"F37.opExtrude","CAP_FACE",FACE,{"disambiguationData":[OSD([sQuery(id+"F36.wireOp",EDGE,"E40"),sQuery(id+"F36.wireOp",EDGE,"E41"),sQuery(id+"F36.wireOp",EDGE,"E48.1.0"),sQuery(id+"F36.wireOp",EDGE,"E48.1.1")])],"isStart":false})});
            var Q1;
            Q1=makeQuery(id+"F37.boolean.opBoolean","COPY",FACE,{"derivedFrom":makeQuery(id+"F37.opExtrude","CAP_FACE",FACE,{"disambiguationData":[OSD([sQuery(id+"F36.wireOp",EDGE,"E40"),sQuery(id+"F36.wireOp",EDGE,"E41"),sQuery(id+"F36.wireOp",EDGE,"E45.trimOffspring"),sQuery(id+"F36.wireOp",EDGE,"E46.trimOffspring")])],"isStart":false})});
            var Q2;
            Q2=makeQuery(id+"F37.boolean.opBoolean","COPY",FACE,{"derivedFrom":makeQuery(id+"F37.opExtrude","CAP_FACE",FACE,{"disambiguationData":[OSD([sQuery(id+"F36.wireOp",EDGE,"E40"),sQuery(id+"F36.wireOp",EDGE,"E41"),sQuery(id+"F36.wireOp",EDGE,"E48.7.0"),sQuery(id+"F36.wireOp",EDGE,"E48.7.1")])],"isStart":false})});
            var Q3;
            Q3=makeQuery(id+"F37.boolean.opBoolean","COPY",FACE,{"derivedFrom":makeQuery(id+"F37.opExtrude","CAP_FACE",FACE,{"disambiguationData":[OSD([sQuery(id+"F36.wireOp",EDGE,"E40"),sQuery(id+"F36.wireOp",EDGE,"E41"),sQuery(id+"F36.wireOp",EDGE,"E48.6.0"),sQuery(id+"F36.wireOp",EDGE,"E48.6.1")])],"isStart":false})});
            var Q4;
            Q4=makeQuery(id+"F37.boolean.opBoolean","COPY",FACE,{"derivedFrom":makeQuery(id+"F37.opExtrude","CAP_FACE",FACE,{"disambiguationData":[OSD([sQuery(id+"F36.wireOp",EDGE,"E40"),sQuery(id+"F36.wireOp",EDGE,"E41"),sQuery(id+"F36.wireOp",EDGE,"E48.5.0"),sQuery(id+"F36.wireOp",EDGE,"E48.5.1")])],"isStart":false})});
            var Q5;
            Q5=makeQuery(id+"F37.boolean.opBoolean","COPY",FACE,{"derivedFrom":makeQuery(id+"F37.opExtrude","CAP_FACE",FACE,{"disambiguationData":[OSD([sQuery(id+"F36.wireOp",EDGE,"E40"),sQuery(id+"F36.wireOp",EDGE,"E41"),sQuery(id+"F36.wireOp",EDGE,"E48.4.0"),sQuery(id+"F36.wireOp",EDGE,"E48.4.1")])],"isStart":false})});
            var Q6;
            Q6=makeQuery(id+"F37.boolean.opBoolean","COPY",FACE,{"derivedFrom":makeQuery(id+"F37.opExtrude","CAP_FACE",FACE,{"disambiguationData":[OSD([sQuery(id+"F36.wireOp",EDGE,"E40"),sQuery(id+"F36.wireOp",EDGE,"E41"),sQuery(id+"F36.wireOp",EDGE,"E48.3.0"),sQuery(id+"F36.wireOp",EDGE,"E48.3.1")])],"isStart":false})});
            var Q7;
            Q7=makeQuery(id+"F37.boolean.opBoolean","COPY",FACE,{"derivedFrom":makeQuery(id+"F37.opExtrude","CAP_FACE",FACE,{"disambiguationData":[OSD([sQuery(id+"F36.wireOp",EDGE,"E40"),sQuery(id+"F36.wireOp",EDGE,"E41"),sQuery(id+"F36.wireOp",EDGE,"E48.2.0"),sQuery(id+"F36.wireOp",EDGE,"E48.2.1")])],"isStart":false})});
            chamfer(context, id + "F38", {"entities" : qUnion([Q0, Q1, Q2, Q3, Q4, Q5, Q6, Q7]), "width" : 0.25 * mm, "tangentPropagation" : true});
        }
    });
